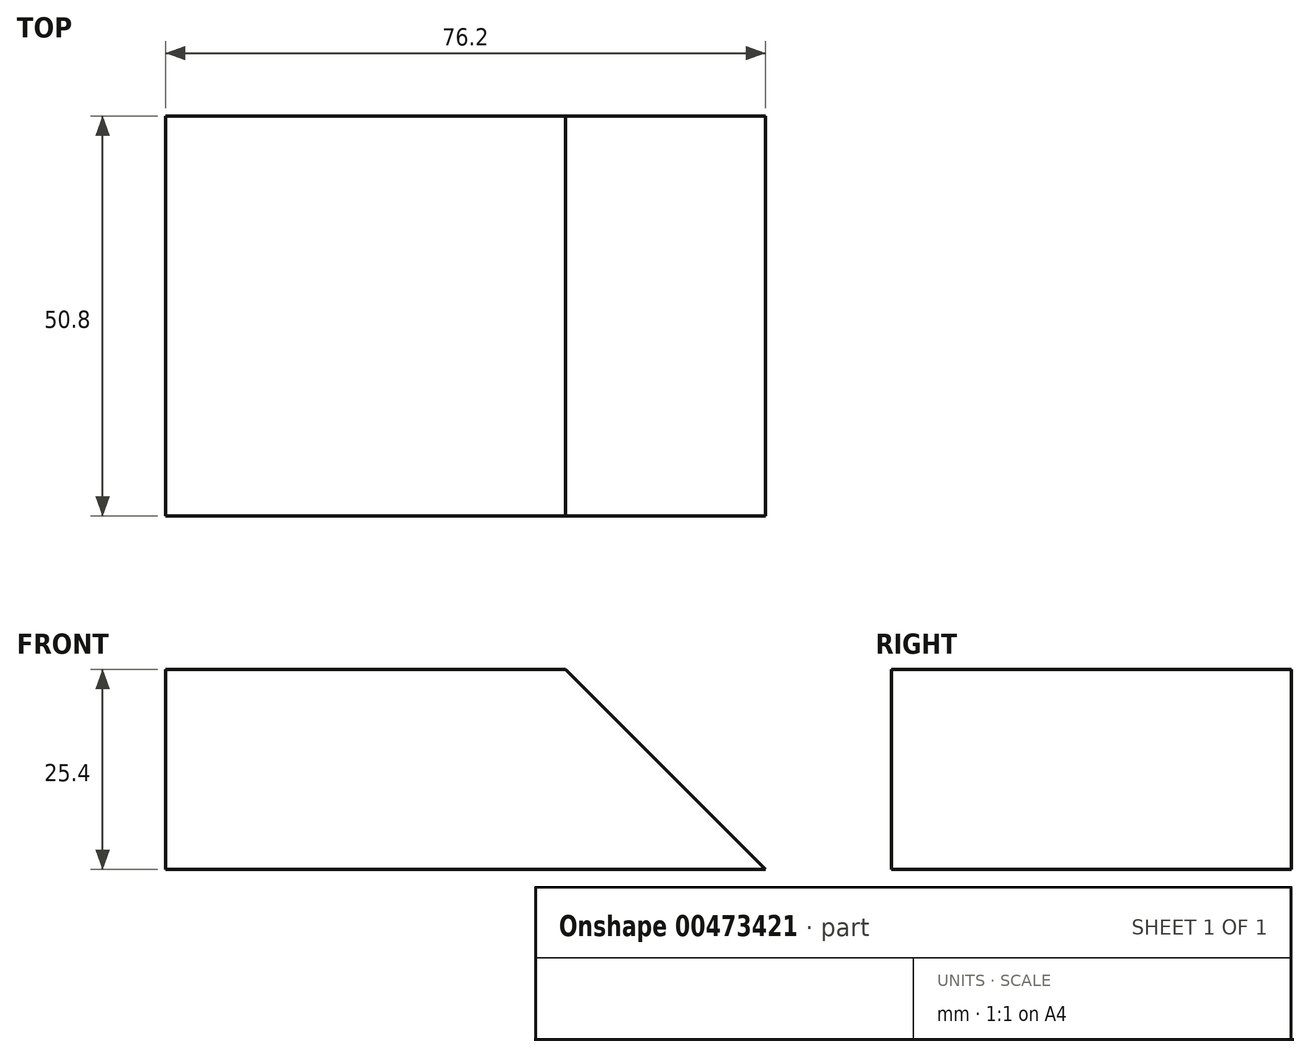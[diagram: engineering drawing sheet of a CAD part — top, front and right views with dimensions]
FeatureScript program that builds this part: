
annotation { "Feature Type Name" : "Feature", "Feature Type Description" : "" }
export const myFeature = defineFeature(function(context is Context, id is Id, definition is map)
    precondition{}
    {
        {
            var Q0;
            Q0=qCreatedBy(makeId("Front.planeOp"),FACE);
            var sketch = newSketch(context, id + "F0", { "sketchPlane" : qUnion([Q0])});
            skLineSegment(sketch, "E0", {"start": v(0, 0) * mm, "end": v(-50.8, 0) * mm});
            skLineSegment(sketch, "E1", {"start": v(-50.8, 0) * mm, "end": v(-50.8, -25.4) * mm});
            skLineSegment(sketch, "E2", {"start": v(-50.8, -25.4) * mm, "end": v(25.4, -25.4) * mm});
            skLineSegment(sketch, "E3", {"start": v(25.4, -25.4) * mm, "end": v(0, 0) * mm});
            skSolve(sketch);
        }
        {
            var Q0;
            Q0 = qSketchRegion(id + "F0", true);
            extrude(context, id + "F1", {"entities" : qUnion([Q0]), "depth" : 50.8 * mm});
        }
    });
